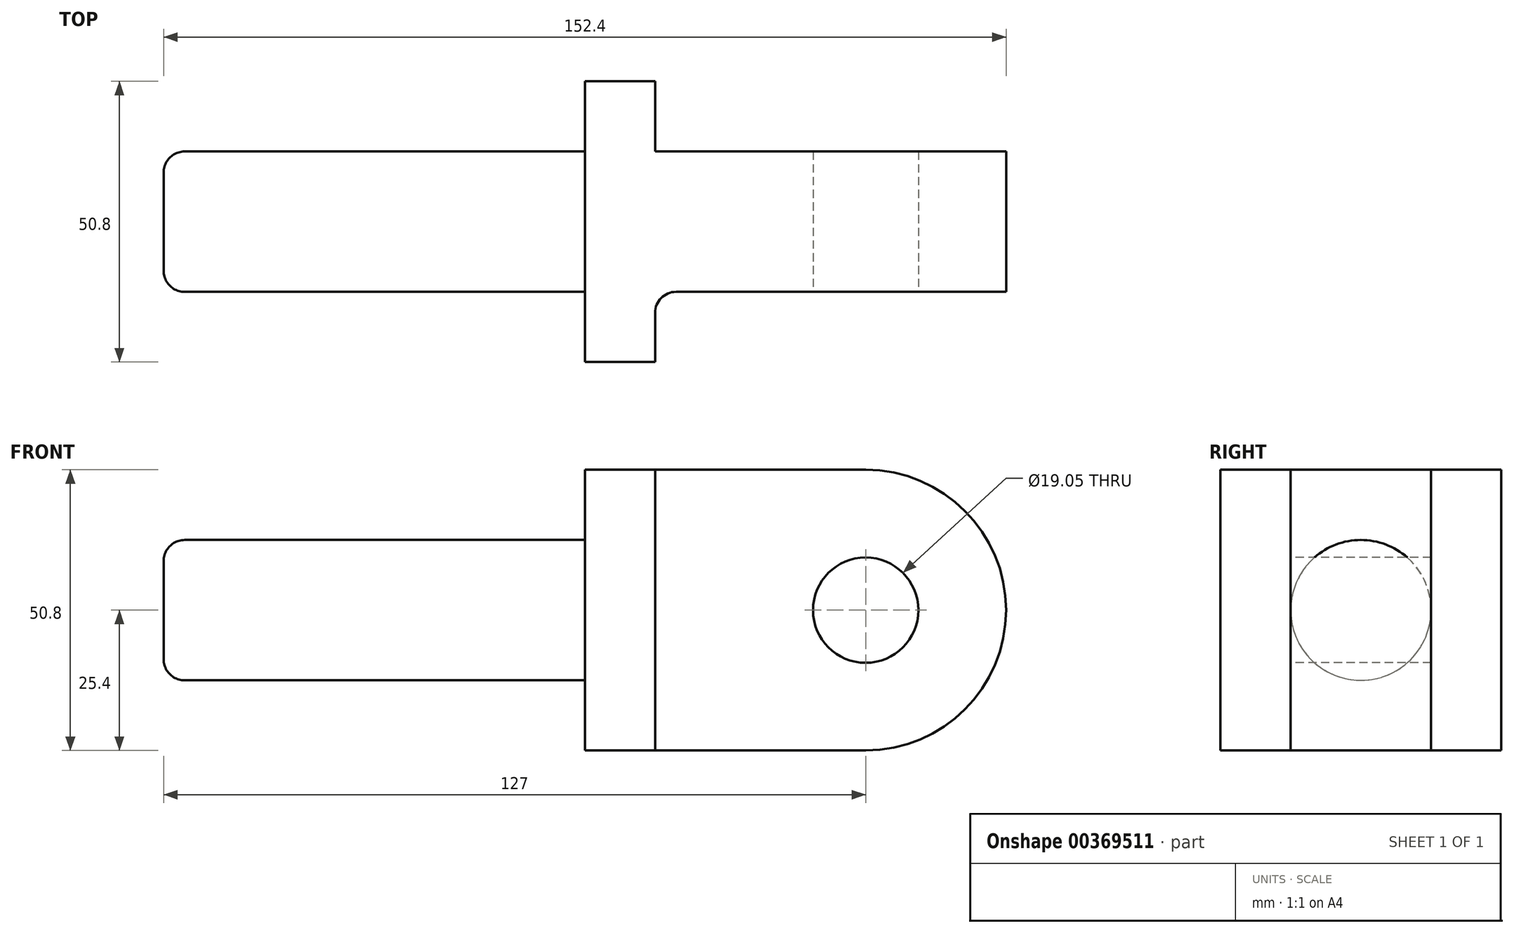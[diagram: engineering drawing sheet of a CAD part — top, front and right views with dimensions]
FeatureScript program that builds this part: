
annotation { "Feature Type Name" : "Feature", "Feature Type Description" : "" }
export const myFeature = defineFeature(function(context is Context, id is Id, definition is map)
    precondition{}
    {
        {
            var Q0;
            Q0=qCreatedBy(makeId("Right.planeOp"),FACE);
            var sketch = newSketch(context, id + "F0", { "sketchPlane" : qUnion([Q0])});
            skLineSegment(sketch, "E0.bottom", {"start": v(25.4, -25.4) * mm, "end": v(-25.4, -25.4) * mm});
            skLineSegment(sketch, "E0.top", {"start": v(25.4, 25.4) * mm, "end": v(-25.4, 25.4) * mm});
            skLineSegment(sketch, "E0.left", {"start": v(25.4, -25.4) * mm, "end": v(25.4, 25.4) * mm});
            skLineSegment(sketch, "E0.right", {"start": v(-25.4, -25.4) * mm, "end": v(-25.4, 25.4) * mm});
            skPoint(sketch, "E0.middle", {"position": v(0, 0) * mm});
            skSolve(sketch);
        }
        {
            var Q0;
            Q0 = qSketchRegion(id + "F0", true);
            extrude(context, id + "F1", {"entities" : qUnion([Q0]), "depth" : 12.7 * mm});
        }
        {
            var Q0;
            Q0=makeQuery(id+"F1.opExtrude","CAP_FACE",FACE,{"disambiguationData":[OSD([sQuery(id+"F0.wireOp",EDGE,"E0.bottom"),sQuery(id+"F0.wireOp",EDGE,"E0.top"),sQuery(id+"F0.wireOp",EDGE,"E0.left"),sQuery(id+"F0.wireOp",EDGE,"E0.right")])],"isStart":true});
            var sketch = newSketch(context, id + "F2", { "sketchPlane" : qUnion([Q0])});
            skCircle(sketch, "E1", {"center": v(0, 0) * mm, "radius": 12.7 * mm});
            skSolve(sketch);
        }
        {
            var Q0;
            Q0=makeQuery(id+"F2.imprint","IMPRINT",FACE,{"disambiguationData":[TD([[makeQuery(id+"F2.imprint","IMPRINT",EDGE,{"derivedFrom":sQuery(id+"F2.wireOp",EDGE,"E1")}),1.0]])]});
            extrude(context, id + "F3", {"entities" : qUnion([Q0]), "operationType" : NewBodyOperationType.ADD, "depth" : 76.2 * mm});
        }
        {
            var Q0;
            Q0=makeQuery(id+"F1.opExtrude","SWEPT_FACE",FACE,{"disambiguationData":[OSD([sQuery(id+"F0.wireOp",EDGE,"E0.right")])]});
            var sketch = newSketch(context, id + "F4", { "sketchPlane" : qUnion([Q0])});
            skLineSegment(sketch, "E2", {"start": v(12.7, 25.4) * mm, "end": v(50.8, 25.4) * mm});
            skLineSegment(sketch, "E3", {"start": v(12.7, -25.4) * mm, "end": v(50.8, -25.4) * mm});
            skArc(sketch, "E4", {"start": v(50.8, -25.4) * mm, "mid": v(76.2, 0) * mm, "end": v(50.8, 25.4) * mm});
            skCircle(sketch, "E5", {"center": v(50.8, 0) * mm, "radius": 9.53 * mm});
            skSolve(sketch);
        }
        {
            var Q0;
            Q0=makeQuery(id+"F4.imprint","IMPRINT",FACE,{"disambiguationData":[TD([[makeQuery(id+"F4.imprint","IMPRINT",EDGE,{"derivedFrom":sQuery(id+"F4.wireOp",EDGE,"E2")}),-1.0]])]});
            extrude(context, id + "F5", {"entities" : qUnion([Q0]), "operationType" : NewBodyOperationType.ADD, "oppositeDirection" : true, "depth" : 38.1 * mm});
        }
        {
            var Q0;
            Q0=makeQuery(id+"F4.imprint","IMPRINT",FACE,{"disambiguationData":[TD([[makeQuery(id+"F4.imprint","IMPRINT",EDGE,{"derivedFrom":sQuery(id+"F4.wireOp",EDGE,"E2")}),-1.0]])]});
            extrude(context, id + "F6", {"entities" : qUnion([Q0]), "operationType" : NewBodyOperationType.REMOVE, "oppositeDirection" : true, "depth" : 12.7 * mm});
        }
        {
            var Q0;
            Q0=makeQuery(id+"F3.opExtrude","CAP_EDGE",EDGE,{"disambiguationData":[OSD([sQuery(id+"F2.wireOp",EDGE,"E1")])],"isStart":false});
            var Q1;
            Q1=makeQuery(id+"F3.opExtrude","CAP_EDGE",EDGE,{"disambiguationData":[OSD([sQuery(id+"F2.wireOp",EDGE,"E1")])],"isStart":true});
            var Q2;
            Q2=makeQuery(id+"F5.opExtrude","CAP_EDGE",EDGE,{"disambiguationData":[OSD([sQuery(id+"F0.wireOp",EDGE,"E0.right")])],"isStart":false});
            var Q3;
            Q3=makeQuery(id+"F6.boolean.opBoolean","COPY",EDGE,{"derivedFrom":makeQuery(id+"F6.opExtrude","CAP_EDGE",EDGE,{"disambiguationData":[OSD([sQuery(id+"F0.wireOp",EDGE,"E0.right")])],"isStart":false})});
            fillet(context, id + "F7", {"entities" : qUnion([Q0, Q1, Q2, Q3]), "radius" : 3.8 * mm, "tangentPropagation" : true, "allowEdgeOverflow" : false});
        }
    });
